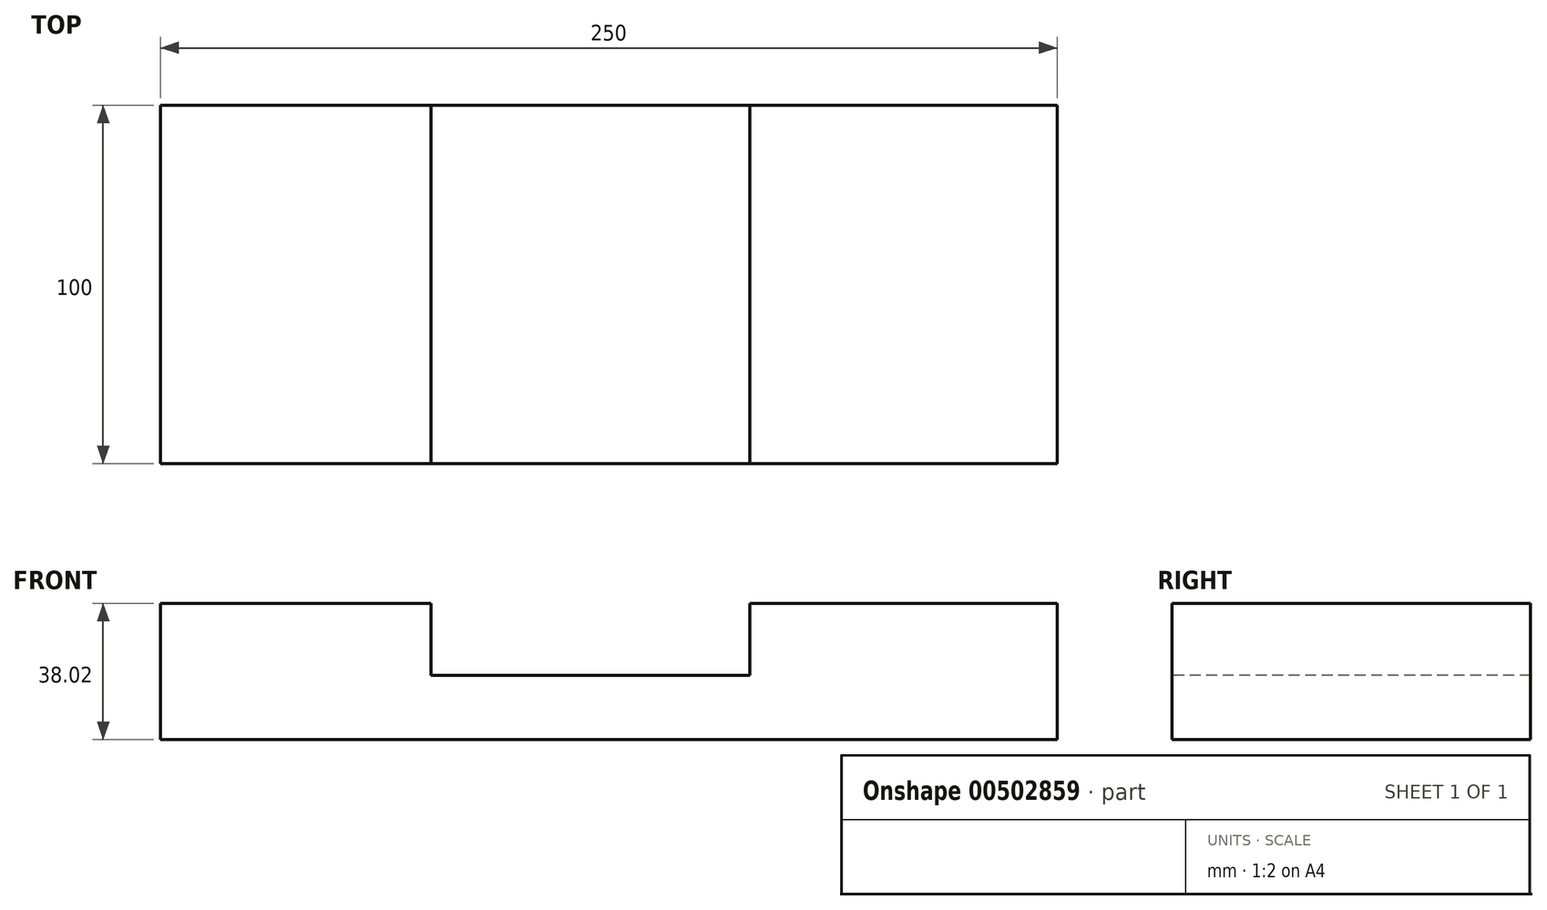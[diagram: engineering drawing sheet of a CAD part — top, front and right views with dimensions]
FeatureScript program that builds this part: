
annotation { "Feature Type Name" : "Feature", "Feature Type Description" : "" }
export const myFeature = defineFeature(function(context is Context, id is Id, definition is map)
    precondition{}
    {
        {
            var Q0;
            Q0=qCreatedBy(makeId("Front.planeOp"),FACE);
            var sketch = newSketch(context, id + "F0", { "sketchPlane" : qUnion([Q0])});
            skLineSegment(sketch, "E0.bottom", {"start": v(-119.9, -25.4) * mm, "end": v(130.1, -25.4) * mm});
            skLineSegment(sketch, "E0.top", {"start": v(-119.9, -43.42) * mm, "end": v(130.1, -43.42) * mm});
            skLineSegment(sketch, "E0.left", {"start": v(-119.9, -25.4) * mm, "end": v(-119.9, -43.42) * mm});
            skLineSegment(sketch, "E0.right", {"start": v(130.1, -25.4) * mm, "end": v(130.1, -43.42) * mm});
            skSolve(sketch);
        }
        {
            var Q0;
            Q0=makeQuery(id+"F0.imprint","IMPRINT",FACE,{"disambiguationData":[TD([[makeQuery(id+"F0.imprint","IMPRINT",EDGE,{"derivedFrom":sQuery(id+"F0.wireOp",EDGE,"E0.bottom")}),-1.0]])]});
            extrude(context, id + "F1", {"entities" : qUnion([Q0]), "endBound" : BoundingType.SYMMETRIC, "depth" : 100 * mm});
        }
        {
            var Q0;
            Q0=makeQuery(id+"F1.opExtrude","SWEPT_FACE",FACE,{"disambiguationData":[OSD([sQuery(id+"F0.wireOp",EDGE,"E0.bottom")])]});
            var sketch = newSketch(context, id + "F2", { "sketchPlane" : qUnion([Q0])});
            skLineSegment(sketch, "E1.bottom", {"start": v(-119.9, 50) * mm, "end": v(-44.45, 50) * mm});
            skLineSegment(sketch, "E1.top", {"start": v(-119.9, -50) * mm, "end": v(-44.45, -50) * mm});
            skLineSegment(sketch, "E1.left", {"start": v(-119.9, 50) * mm, "end": v(-119.9, -50) * mm});
            skLineSegment(sketch, "E1.right", {"start": v(-44.45, 50) * mm, "end": v(-44.45, -50) * mm});
            skLineSegment(sketch, "E2.bottom", {"start": v(130.1, 50) * mm, "end": v(44.45, 50) * mm});
            skLineSegment(sketch, "E2.top", {"start": v(130.1, -50) * mm, "end": v(44.45, -50) * mm});
            skLineSegment(sketch, "E2.left", {"start": v(130.1, 50) * mm, "end": v(130.1, -50) * mm});
            skLineSegment(sketch, "E2.right", {"start": v(44.45, 50) * mm, "end": v(44.45, -50) * mm});
            skLineSegment(sketch, "E3.bottom", {"start": v(0, 50) * mm, "end": v(-44.45, 50) * mm});
            skLineSegment(sketch, "E3.top", {"start": v(0, -50) * mm, "end": v(-44.45, -50) * mm});
            skLineSegment(sketch, "E3.left", {"start": v(0, 50) * mm, "end": v(0, -50) * mm});
            skLineSegment(sketch, "E4.bottom", {"start": v(0, 50) * mm, "end": v(44.45, 50) * mm});
            skLineSegment(sketch, "E4.top", {"start": v(0, -50) * mm, "end": v(44.45, -50) * mm});
            skSolve(sketch);
        }
        {
            var Q0;
            Q0=makeQuery(id+"F2.imprint","IMPRINT",FACE,{"disambiguationData":[TD([[makeQuery(id+"F2.imprint","IMPRINT",EDGE,{"derivedFrom":sQuery(id+"F2.wireOp",EDGE,"E1.bottom")}),-1.0]])]});
            var Q1;
            Q1=makeQuery(id+"F2.imprint","IMPRINT",FACE,{"disambiguationData":[TD([[makeQuery(id+"F2.imprint","IMPRINT",EDGE,{"derivedFrom":sQuery(id+"F2.wireOp",EDGE,"E2.bottom")}),-1.0]])]});
            extrude(context, id + "F3", {"entities" : qUnion([Q0, Q1]), "operationType" : NewBodyOperationType.ADD, "depth" : 20 * mm});
        }
    });
